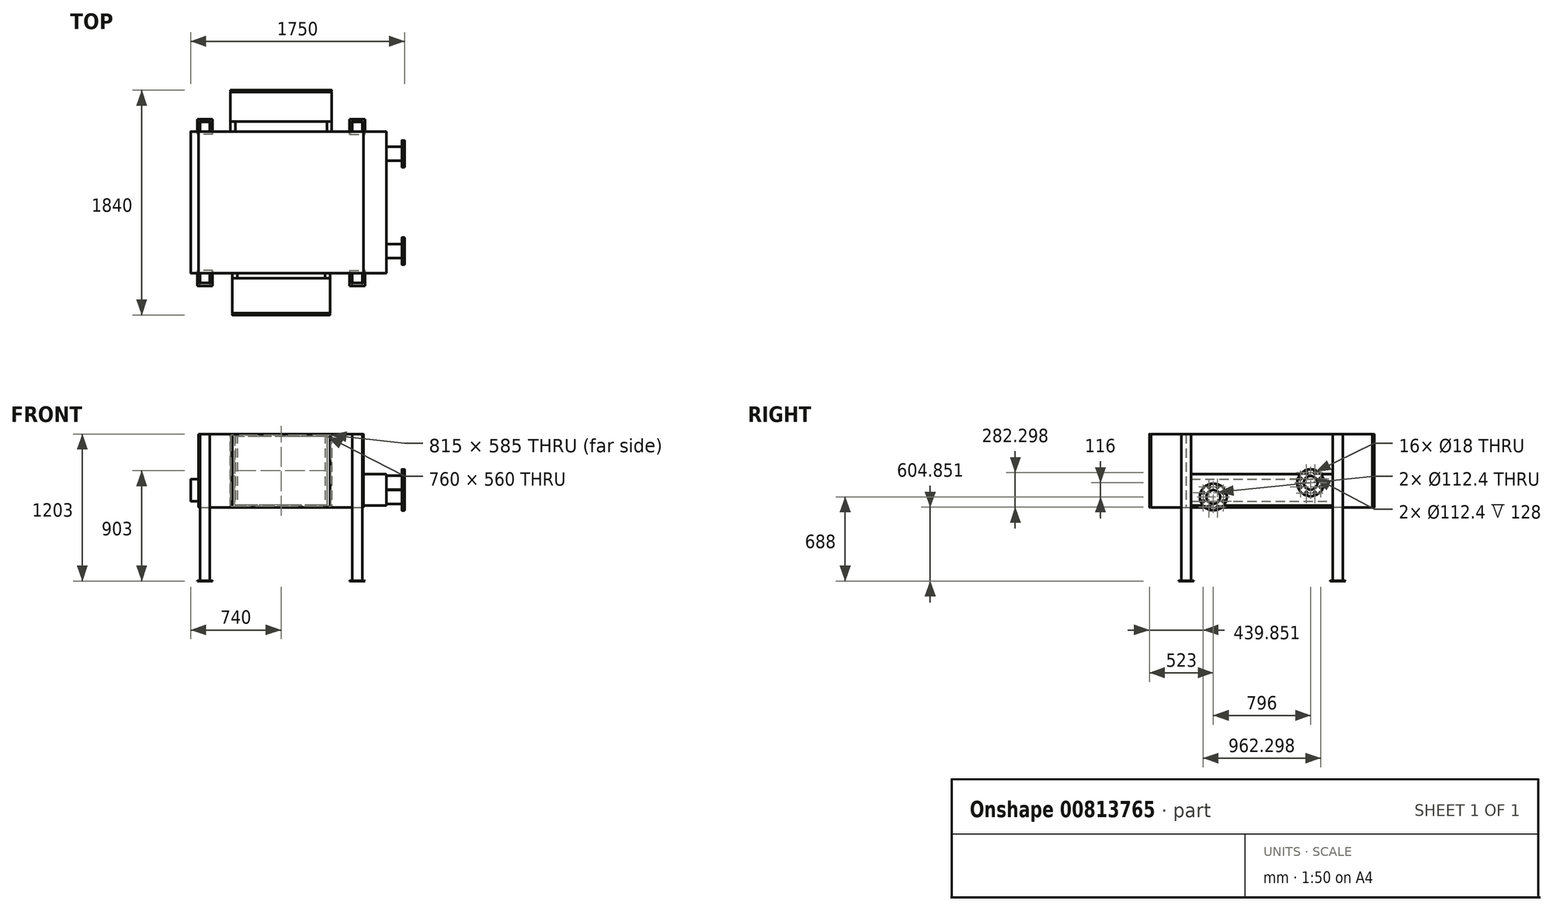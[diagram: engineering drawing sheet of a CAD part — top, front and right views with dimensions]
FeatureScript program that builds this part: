
annotation { "Feature Type Name" : "Feature", "Feature Type Description" : "" }
export const myFeature = defineFeature(function(context is Context, id is Id, definition is map)
    precondition{}
    {
        {
            var Q0;
            Q0=qCreatedBy(makeId("Top.planeOp"),FACE);
            var sketch = newSketch(context, id + "F0", { "sketchPlane" : qUnion([Q0])});
            skLineSegment(sketch, "E0.bottom", {"start": v(0, 0) * mm, "end": v(1350, 0) * mm});
            skLineSegment(sketch, "E0.top", {"start": v(0, 1160) * mm, "end": v(1350, 1160) * mm});
            skLineSegment(sketch, "E0.left", {"start": v(0, 0) * mm, "end": v(0, 1160) * mm});
            skLineSegment(sketch, "E0.right", {"start": v(1350, 0) * mm, "end": v(1350, 1160) * mm});
            skSolve(sketch);
        }
        {
            var Q0;
            Q0 = qSketchRegion(id + "F0", true);
            extrude(context, id + "F1", {"entities" : qUnion([Q0]), "depth" : 600 * mm, "offsetDistance" : 25 * mm});
        }
        {
            var Q0;
            Q0=makeQuery(id+"F1.opExtrude","SWEPT_FACE",FACE,{"disambiguationData":[OSD([sQuery(id+"F0.wireOp",EDGE,"E0.bottom")])]});
            var sketch = newSketch(context, id + "F2", { "sketchPlane" : qUnion([Q0])});
            skLineSegment(sketch, "E1.bottom", {"start": v(1258, -600) * mm, "end": v(1338, -600) * mm});
            skLineSegment(sketch, "E1.top", {"start": v(1258, 600) * mm, "end": v(1338, 600) * mm});
            skLineSegment(sketch, "E1.left", {"start": v(1258, -600) * mm, "end": v(1258, 600) * mm});
            skLineSegment(sketch, "E1.right", {"start": v(1338, -600) * mm, "end": v(1338, 600) * mm});
            skLineSegment(sketch, "E2", {"start": v(675, 600) * mm, "end": v(675, 2551.14) * mm, "construction": true});
            skLineSegment(sketch, "E3.MirrorCS", {"start": v(92, -600) * mm, "end": v(12, -600) * mm});
            skLineSegment(sketch, "E4.MirrorCS", {"start": v(92, 600) * mm, "end": v(12, 600) * mm});
            skLineSegment(sketch, "E5.MirrorCS", {"start": v(92, -600) * mm, "end": v(92, 600) * mm});
            skLineSegment(sketch, "E6.MirrorCS", {"start": v(12, -600) * mm, "end": v(12, 600) * mm});
            skSolve(sketch);
        }
        {
            var Q0;
            {var subQ0=sQuery(id+"F2.wireOp",EDGE,"E3.MirrorCS");Q0=makeQuery(id+"F2.imprint","IMPRINT",FACE,{"disambiguationData":[TD([[makeQuery(id+"F2.imprint","IMPRINT",EDGE,{"derivedFrom":subQ0}),-1.0]])]});}
            var Q1;
            {var subQ0=sQuery(id+"F2.wireOp",EDGE,"E1.bottom");Q1=makeQuery(id+"F2.imprint","IMPRINT",FACE,{"disambiguationData":[TD([[makeQuery(id+"F2.imprint","IMPRINT",EDGE,{"derivedFrom":subQ0}),1.0]])]});}
            var Q2;
            {var subQ0=sQuery(id+"F2.wireOp",EDGE,"E1.top");Q2=makeQuery(id+"F2.imprint","IMPRINT",FACE,{"disambiguationData":[TD([[makeQuery(id+"F2.imprint","IMPRINT",EDGE,{"derivedFrom":subQ0}),-1.0]])]});}
            var Q3;
            {var subQ0=sQuery(id+"F2.wireOp",EDGE,"E4.MirrorCS");Q3=makeQuery(id+"F2.imprint","IMPRINT",FACE,{"disambiguationData":[TD([[makeQuery(id+"F2.imprint","IMPRINT",EDGE,{"derivedFrom":subQ0}),-1.0]])]});}
            extrude(context, id + "F3", {"entities" : qUnion([Q0, Q1, Q2, Q3]), "depth" : 80 * mm, "offsetDistance" : 25 * mm});
        }
        {
            var Q0;
            Q0=makeQuery(id+"F1.opExtrude","CAP_EDGE",EDGE,{"disambiguationData":[OSD([sQuery(id+"F0.wireOp",EDGE,"E0.right")])],"isStart":false});
            cPlane(context, id + "F4", {"entities" : qUnion([Q0]), "cplaneType" : CPlaneType.MID_PLANE, "offset" : 25 * mm, "width" : 150 * mm, "height" : 150 * mm});
        }
        {
            var Q0;
            Q0=makeQuery(id+"F3.opExtrude","SWEPT_BODY",BODY,{"disambiguationData":[OSD([sQuery(id+"F2.wireOp",EDGE,"E3.MirrorCS"),sQuery(id+"F2.wireOp",EDGE,"E4.MirrorCS"),sQuery(id+"F2.wireOp",EDGE,"E5.MirrorCS"),sQuery(id+"F2.wireOp",EDGE,"E6.MirrorCS")])]});
            var Q1;
            Q1=makeQuery(id+"F3.opExtrude","SWEPT_BODY",BODY,{"disambiguationData":[OSD([sQuery(id+"F2.wireOp",EDGE,"E1.bottom"),sQuery(id+"F2.wireOp",EDGE,"E1.top"),sQuery(id+"F2.wireOp",EDGE,"E1.left"),sQuery(id+"F2.wireOp",EDGE,"E1.right")])]});
            var Q2;
            Q2=qCreatedBy(id+"F4.planeOp",FACE);
            mirror(context, id + "F5", {"entities" : qUnion([Q0, Q1]), "mirrorPlane" : qUnion([Q2])});
        }
        {
            var Q0;
            Q0=makeQuery(id+"F3.opExtrude","SWEPT_FACE",FACE,{"disambiguationData":[OSD([sQuery(id+"F2.wireOp",EDGE,"E1.bottom")])]});
            var sketch = newSketch(context, id + "F6", { "sketchPlane" : qUnion([Q0])});
            skLineSegment(sketch, "E7", {"start": v(1338, 80) * mm, "end": v(1258, 0) * mm, "construction": true});
            skLineSegment(sketch, "E8", {"start": v(1258, 0) * mm, "end": v(1338, 0) * mm, "construction": true});
            skLineSegment(sketch, "E9", {"start": v(1338, 0) * mm, "end": v(1258, 80) * mm, "construction": true});
            skLineSegment(sketch, "E10.0", {"start": v(1350, 0) * mm, "end": v(1350, -1160) * mm, "construction": true});
            skLineSegment(sketch, "E11.0", {"start": v(0, 0) * mm, "end": v(0, -1160) * mm, "construction": true});
            skLineSegment(sketch, "E12.0", {"start": v(0, -1160) * mm, "end": v(1350, -1160) * mm, "construction": true});
            skLineSegment(sketch, "E13.0", {"start": v(0, 0) * mm, "end": v(1350, 0) * mm, "construction": true});
            skLineSegment(sketch, "E14", {"start": v(675, -1160) * mm, "end": v(675, 174.46) * mm, "construction": true});
            skLineSegment(sketch, "E15", {"start": v(1350, -580) * mm, "end": v(-372.2, -580) * mm, "construction": true});
            skLineSegment(sketch, "E16.bottom", {"start": v(1235.5, -22.5) * mm, "end": v(1360.5, -22.5) * mm});
            skLineSegment(sketch, "E16.top", {"start": v(1235.5, 102.5) * mm, "end": v(1360.5, 102.5) * mm});
            skLineSegment(sketch, "E16.left", {"start": v(1235.5, -22.5) * mm, "end": v(1235.5, 102.5) * mm});
            skLineSegment(sketch, "E16.right", {"start": v(1360.5, -22.5) * mm, "end": v(1360.5, 102.5) * mm});
            skPoint(sketch, "E16.middle", {"position": v(1298, 40) * mm});
            skLineSegment(sketch, "E17.MirrorCS", {"start": v(1338, -1240) * mm, "end": v(1258, -1160) * mm, "construction": true});
            skLineSegment(sketch, "E18.MirrorCS", {"start": v(1235.5, -1137.5) * mm, "end": v(1360.5, -1137.5) * mm});
            skLineSegment(sketch, "E19.MirrorCS", {"start": v(1235.5, -1262.5) * mm, "end": v(1360.5, -1262.5) * mm});
            skLineSegment(sketch, "E20.MirrorCS", {"start": v(1235.5, -1137.5) * mm, "end": v(1235.5, -1262.5) * mm});
            skLineSegment(sketch, "E21.MirrorCS", {"start": v(1338, -1160) * mm, "end": v(1258, -1240) * mm, "construction": true});
            skLineSegment(sketch, "E22.MirrorCS", {"start": v(1258, -1160) * mm, "end": v(1338, -1160) * mm, "construction": true});
            skLineSegment(sketch, "E23.MirrorCS", {"start": v(1360.5, -1137.5) * mm, "end": v(1360.5, -1262.5) * mm});
            skPoint(sketch, "E24.MirrorP", {"position": v(1298, -1200) * mm});
            skLineSegment(sketch, "E25.MirrorCS", {"start": v(-10.5, -22.5) * mm, "end": v(-10.5, 102.5) * mm});
            skLineSegment(sketch, "E26.MirrorCS", {"start": v(114.5, 102.5) * mm, "end": v(-10.5, 102.5) * mm});
            skLineSegment(sketch, "E27.MirrorCS", {"start": v(114.5, -22.5) * mm, "end": v(-10.5, -22.5) * mm});
            skLineSegment(sketch, "E28.MirrorCS", {"start": v(12, 0) * mm, "end": v(92, 80) * mm, "construction": true});
            skLineSegment(sketch, "E29.MirrorCS", {"start": v(92, 0) * mm, "end": v(12, 0) * mm, "construction": true});
            skLineSegment(sketch, "E30.MirrorCS", {"start": v(12, 80) * mm, "end": v(92, 0) * mm, "construction": true});
            skLineSegment(sketch, "E31.MirrorCS", {"start": v(114.5, -1137.5) * mm, "end": v(114.5, -1262.5) * mm});
            skLineSegment(sketch, "E32.MirrorCS", {"start": v(114.5, -1137.5) * mm, "end": v(-10.5, -1137.5) * mm});
            skLineSegment(sketch, "E33.MirrorCS", {"start": v(92, -1160) * mm, "end": v(12, -1160) * mm, "construction": true});
            skLineSegment(sketch, "E34.MirrorCS", {"start": v(-10.5, -1137.5) * mm, "end": v(-10.5, -1262.5) * mm});
            skLineSegment(sketch, "E35.MirrorCS", {"start": v(114.5, -22.5) * mm, "end": v(114.5, 102.5) * mm});
            skLineSegment(sketch, "E36.MirrorCS", {"start": v(12, -1160) * mm, "end": v(92, -1240) * mm, "construction": true});
            skPoint(sketch, "E37.MirrorP", {"position": v(52, 40) * mm});
            skLineSegment(sketch, "E38.MirrorCS", {"start": v(114.5, -1262.5) * mm, "end": v(-10.5, -1262.5) * mm});
            skLineSegment(sketch, "E39.MirrorCS", {"start": v(12, -1240) * mm, "end": v(92, -1160) * mm, "construction": true});
            skPoint(sketch, "E40.MirrorP", {"position": v(52, -1200) * mm});
            skSolve(sketch);
        }
        {
            var Q0;
            Q0 = qSketchRegion(id + "F6", true);
            extrude(context, id + "F7", {"entities" : qUnion([Q0]), "operationType" : NewBodyOperationType.ADD, "depth" : 3 * mm, "offsetDistance" : 25 * mm});
        }
        {
            var Q0;
            Q0=makeQuery(id+"F1.opExtrude","SWEPT_FACE",FACE,{"disambiguationData":[OSD([sQuery(id+"F0.wireOp",EDGE,"E0.bottom")])]});
            var sketch = newSketch(context, id + "F8", { "sketchPlane" : qUnion([Q0])});
            skLineSegment(sketch, "E41", {"start": v(675, 600) * mm, "end": v(675, 0) * mm, "construction": true});
            skLineSegment(sketch, "E42.bottom", {"start": v(1075, 600) * mm, "end": v(275, 600) * mm});
            skLineSegment(sketch, "E42.top", {"start": v(1075, 0) * mm, "end": v(275, 0) * mm});
            skLineSegment(sketch, "E42.left", {"start": v(1075, 600) * mm, "end": v(1075, 0) * mm});
            skLineSegment(sketch, "E42.right", {"start": v(275, 600) * mm, "end": v(275, 0) * mm});
            skPoint(sketch, "E42.middle", {"position": v(675, 300) * mm});
            skLineSegment(sketch, "E43.0", {"start": v(316, 600) * mm, "end": v(316, 0) * mm});
            skLineSegment(sketch, "E44.0", {"start": v(-5, -5) * mm, "end": v(1355, -5) * mm});
            skLineSegment(sketch, "E44.1", {"start": v(-5, 605) * mm, "end": v(-5, -5) * mm});
            skLineSegment(sketch, "E44.2", {"start": v(1355, 605) * mm, "end": v(-5, 605) * mm});
            skLineSegment(sketch, "E44.3", {"start": v(1355, -5) * mm, "end": v(1355, 605) * mm});
            skLineSegment(sketch, "E45.0", {"start": v(1034, 600) * mm, "end": v(1034, 0) * mm});
            skSolve(sketch);
        }
        {
            var Q0;
            {var subQ0=sQuery(id+"F8.wireOp",EDGE,"E42.right");Q0=makeQuery(id+"F8.imprint","IMPRINT",FACE,{"disambiguationData":[TD([[makeQuery(id+"F8.imprint","IMPRINT",EDGE,{"derivedFrom":subQ0}),1.0]])]});}
            var Q1;
            {var subQ0=sQuery(id+"F8.wireOp",EDGE,"E42.left");Q1=makeQuery(id+"F8.imprint","IMPRINT",FACE,{"disambiguationData":[TD([[makeQuery(id+"F8.imprint","IMPRINT",EDGE,{"derivedFrom":subQ0}),-1.0]])]});}
            extrude(context, id + "F9", {"entities" : qUnion([Q0, Q1]), "depth" : 41 * mm, "offsetDistance" : 25 * mm});
        }
        {
            var Q0;
            Q0=makeQuery(id+"F9.opExtrude","CAP_FACE",FACE,{"disambiguationData":[OSD([sQuery(id+"F8.wireOp",EDGE,"E42.bottom"),sQuery(id+"F8.wireOp",EDGE,"E42.top"),sQuery(id+"F8.wireOp",EDGE,"E42.right"),sQuery(id+"F8.wireOp",EDGE,"E43.0")])],"isStart":false});
            var sketch = newSketch(context, id + "F10", { "sketchPlane" : qUnion([Q0])});
            skLineSegment(sketch, "E46.bottom", {"start": v(275, 600) * mm, "end": v(1075, 600) * mm});
            skLineSegment(sketch, "E46.top", {"start": v(275, 0) * mm, "end": v(1075, 0) * mm});
            skLineSegment(sketch, "E46.left", {"start": v(275, 600) * mm, "end": v(275, 0) * mm});
            skLineSegment(sketch, "E46.right", {"start": v(1075, 600) * mm, "end": v(1075, 0) * mm});
            skSolve(sketch);
        }
        {
            var Q0;
            Q0 = qSketchRegion(id + "F10", true);
            extrude(context, id + "F11", {"entities" : qUnion([Q0]), "depth" : 277 * mm, "offsetDistance" : 25 * mm});
        }
        {
            var Q0;
            Q0=makeQuery(id+"F11.opExtrude","CAP_FACE",FACE,{"disambiguationData":[OSD([sQuery(id+"F10.wireOp",EDGE,"E46.bottom"),sQuery(id+"F10.wireOp",EDGE,"E46.top"),sQuery(id+"F10.wireOp",EDGE,"E46.left"),sQuery(id+"F10.wireOp",EDGE,"E46.right")])],"isStart":false});
            var sketch = newSketch(context, id + "F12", { "sketchPlane" : qUnion([Q0])});
            skLineSegment(sketch, "E47.bottom", {"start": v(275, 600) * mm, "end": v(1075, 600) * mm});
            skLineSegment(sketch, "E47.top", {"start": v(275, 0) * mm, "end": v(1075, 0) * mm});
            skLineSegment(sketch, "E47.left", {"start": v(275, 600) * mm, "end": v(275, 0) * mm});
            skLineSegment(sketch, "E47.right", {"start": v(1075, 600) * mm, "end": v(1075, 0) * mm});
            skSolve(sketch);
        }
        {
            var Q0;
            Q0 = qSketchRegion(id + "F12", true);
            extrude(context, id + "F13", {"entities" : qUnion([Q0]), "operationType" : NewBodyOperationType.ADD, "depth" : 23 * mm, "offsetDistance" : 25 * mm});
        }
        {
            var Q0;
            Q0=makeQuery(id+"F13.opExtrude","CAP_FACE",FACE,{"disambiguationData":[OSD([sQuery(id+"F12.wireOp",EDGE,"E47.bottom"),sQuery(id+"F12.wireOp",EDGE,"E47.top"),sQuery(id+"F12.wireOp",EDGE,"E47.left"),sQuery(id+"F12.wireOp",EDGE,"E47.right")])],"isStart":false});
            cPlane(context, id + "F14", {"entities" : qUnion([Q0]), "cplaneType" : CPlaneType.OFFSET, "offset" : 7.5 * mm, "oppositeDirection" : true, "width" : 150 * mm, "height" : 150 * mm});
        }
        {
            var Q0;
            Q0=qCreatedBy(id+"F14.planeOp",FACE);
            var sketch = newSketch(context, id + "F15", { "sketchPlane" : qUnion([Q0])});
            skLineSegment(sketch, "E48.0", {"start": v(295, 580) * mm, "end": v(295, 20) * mm});
            skLineSegment(sketch, "E48.1", {"start": v(1055, 580) * mm, "end": v(295, 580) * mm});
            skLineSegment(sketch, "E48.2", {"start": v(1055, 20) * mm, "end": v(1055, 580) * mm});
            skLineSegment(sketch, "E48.3", {"start": v(295, 20) * mm, "end": v(1055, 20) * mm});
            skLineSegment(sketch, "E49.0.0", {"start": v(275, 600) * mm, "end": v(275, 0) * mm});
            skLineSegment(sketch, "E49.0.1", {"start": v(275, 0) * mm, "end": v(1075, 0) * mm});
            skLineSegment(sketch, "E49.0.2", {"start": v(1075, 0) * mm, "end": v(1075, 600) * mm});
            skLineSegment(sketch, "E49.0.3", {"start": v(1075, 600) * mm, "end": v(275, 600) * mm});
            skSolve(sketch);
        }
        {
            var Q0;
            Q0=makeQuery(id+"F15.imprint","IMPRINT",FACE,{"disambiguationData":[TD([[makeQuery(id+"F15.imprint","IMPRINT",EDGE,{"derivedFrom":sQuery(id+"F15.wireOp",EDGE,"E48.0")}),-1.0]])]});
            extrude(context, id + "F16", {"entities" : qUnion([Q0]), "operationType" : NewBodyOperationType.REMOVE, "oppositeDirection" : true, "depth" : 7.5 * mm, "offsetDistance" : 25 * mm});
        }
        {
            var Q0;
            Q0=makeQuery(id+"F1.opExtrude","SWEPT_FACE",FACE,{"disambiguationData":[OSD([sQuery(id+"F0.wireOp",EDGE,"E0.top")])]});
            var sketch = newSketch(context, id + "F17", { "sketchPlane" : qUnion([Q0])});
            skLineSegment(sketch, "E50", {"start": v(-675, 0) * mm, "end": v(-675, 783.43) * mm, "construction": true});
            skLineSegment(sketch, "E51.bottom", {"start": v(-1090, 600) * mm, "end": v(-1049, 600) * mm});
            skLineSegment(sketch, "E51.top", {"start": v(-1090, 0) * mm, "end": v(-1049, 0) * mm});
            skLineSegment(sketch, "E51.left", {"start": v(-1090, 600) * mm, "end": v(-1090, 0) * mm});
            skLineSegment(sketch, "E51.right", {"start": v(-1049, 600) * mm, "end": v(-1049, 0) * mm});
            skLineSegment(sketch, "E52.MirrorCS", {"start": v(-301, 600) * mm, "end": v(-301, 0) * mm});
            skLineSegment(sketch, "E53.MirrorCS", {"start": v(-260, 600) * mm, "end": v(-260, 0) * mm});
            skLineSegment(sketch, "E54.MirrorCS", {"start": v(-260, 0) * mm, "end": v(-301, 0) * mm});
            skLineSegment(sketch, "E55.MirrorCS", {"start": v(-260, 600) * mm, "end": v(-301, 600) * mm});
            skSolve(sketch);
        }
        {
            var Q0;
            Q0=makeQuery(id+"F17.imprint","IMPRINT",FACE,{"disambiguationData":[TD([[makeQuery(id+"F17.imprint","IMPRINT",EDGE,{"derivedFrom":sQuery(id+"F17.wireOp",EDGE,"E51.bottom")}),1.0]])]});
            var Q1;
            Q1=makeQuery(id+"F17.imprint","IMPRINT",FACE,{"disambiguationData":[TD([[makeQuery(id+"F17.imprint","IMPRINT",EDGE,{"derivedFrom":sQuery(id+"F17.wireOp",EDGE,"E52.MirrorCS")}),1.0]])]});
            extrude(context, id + "F18", {"entities" : qUnion([Q0, Q1]), "depth" : 81 * mm, "offsetDistance" : 25 * mm});
        }
        {
            var Q0;
            Q0=makeQuery(id+"F18.opExtrude","CAP_FACE",FACE,{"disambiguationData":[OSD([sQuery(id+"F17.wireOp",EDGE,"E51.bottom"),sQuery(id+"F17.wireOp",EDGE,"E51.top"),sQuery(id+"F17.wireOp",EDGE,"E51.left"),sQuery(id+"F17.wireOp",EDGE,"E51.right")])],"isStart":false});
            var sketch = newSketch(context, id + "F19", { "sketchPlane" : qUnion([Q0])});
            skLineSegment(sketch, "E56.bottom", {"start": v(-1090, 600) * mm, "end": v(-260, 600) * mm});
            skLineSegment(sketch, "E56.top", {"start": v(-1090, 0) * mm, "end": v(-260, 0) * mm});
            skLineSegment(sketch, "E56.left", {"start": v(-1090, 600) * mm, "end": v(-1090, 0) * mm});
            skLineSegment(sketch, "E56.right", {"start": v(-260, 600) * mm, "end": v(-260, 0) * mm});
            skSolve(sketch);
        }
        {
            var Q0;
            Q0 = qSketchRegion(id + "F19", true);
            extrude(context, id + "F20", {"entities" : qUnion([Q0]), "depth" : 258 * mm, "offsetDistance" : 25 * mm});
        }
        {
            var Q0;
            Q0=makeQuery(id+"F20.opExtrude","CAP_FACE",FACE,{"disambiguationData":[OSD([sQuery(id+"F19.wireOp",EDGE,"E56.bottom"),sQuery(id+"F19.wireOp",EDGE,"E56.top"),sQuery(id+"F19.wireOp",EDGE,"E56.left"),sQuery(id+"F19.wireOp",EDGE,"E56.right")])],"isStart":false});
            cPlane(context, id + "F21", {"entities" : qUnion([Q0]), "cplaneType" : CPlaneType.OFFSET, "offset" : 7.5 * mm, "oppositeDirection" : true, "width" : 150 * mm, "height" : 150 * mm});
        }
        {
            var Q0;
            Q0=qCreatedBy(id+"F21.planeOp",FACE);
            var sketch = newSketch(context, id + "F22", { "sketchPlane" : qUnion([Q0])});
            skLineSegment(sketch, "E57.0.0", {"start": v(-260, 600) * mm, "end": v(-1090, 600) * mm});
            skLineSegment(sketch, "E57.0.1", {"start": v(-1090, 600) * mm, "end": v(-1090, 0) * mm});
            skLineSegment(sketch, "E57.0.2", {"start": v(-1090, 0) * mm, "end": v(-260, 0) * mm});
            skLineSegment(sketch, "E57.0.3", {"start": v(-260, 0) * mm, "end": v(-260, 600) * mm});
            skLineSegment(sketch, "E58.0", {"start": v(-267.5, 592.5) * mm, "end": v(-1082.5, 592.5) * mm});
            skLineSegment(sketch, "E58.1", {"start": v(-267.5, 7.5) * mm, "end": v(-267.5, 592.5) * mm});
            skLineSegment(sketch, "E58.2", {"start": v(-1082.5, 7.5) * mm, "end": v(-267.5, 7.5) * mm});
            skLineSegment(sketch, "E58.3", {"start": v(-1082.5, 592.5) * mm, "end": v(-1082.5, 7.5) * mm});
            skSolve(sketch);
        }
        {
            var Q0;
            Q0=makeQuery(id+"F22.imprint","IMPRINT",FACE,{"disambiguationData":[TD([[makeQuery(id+"F22.imprint","IMPRINT",EDGE,{"derivedFrom":sQuery(id+"F22.wireOp",EDGE,"E57.0.0")}),1.0]])]});
            extrude(context, id + "F23", {"entities" : qUnion([Q0]), "operationType" : NewBodyOperationType.REMOVE, "oppositeDirection" : true, "depth" : 7.5 * mm, "offsetDistance" : 25 * mm});
        }
        {
            var Q0;
            Q0=makeQuery(id+"F13.opExtrude","CAP_EDGE",EDGE,{"disambiguationData":[OSD([sQuery(id+"F12.wireOp",EDGE,"E47.left")])],"isStart":false});
            var Q1;
            Q1=makeQuery(id+"F13.opExtrude","CAP_EDGE",EDGE,{"disambiguationData":[OSD([sQuery(id+"F12.wireOp",EDGE,"E47.bottom")])],"isStart":false});
            var Q2;
            Q2=makeQuery(id+"F13.opExtrude","CAP_EDGE",EDGE,{"disambiguationData":[OSD([sQuery(id+"F12.wireOp",EDGE,"E47.top")])],"isStart":false});
            var Q3;
            Q3=makeQuery(id+"F13.opExtrude","CAP_EDGE",EDGE,{"disambiguationData":[OSD([sQuery(id+"F12.wireOp",EDGE,"E47.right")])],"isStart":false});
            var Q4;
            Q4=makeQuery(id+"F20.opExtrude","CAP_EDGE",EDGE,{"disambiguationData":[OSD([sQuery(id+"F19.wireOp",EDGE,"E56.left")])],"isStart":false});
            var Q5;
            Q5=makeQuery(id+"F20.opExtrude","CAP_EDGE",EDGE,{"disambiguationData":[OSD([sQuery(id+"F19.wireOp",EDGE,"E56.bottom")])],"isStart":false});
            var Q6;
            Q6=makeQuery(id+"F20.opExtrude","CAP_EDGE",EDGE,{"disambiguationData":[OSD([sQuery(id+"F19.wireOp",EDGE,"E56.right")])],"isStart":false});
            var Q7;
            Q7=makeQuery(id+"F20.opExtrude","CAP_EDGE",EDGE,{"disambiguationData":[OSD([sQuery(id+"F19.wireOp",EDGE,"E56.top")])],"isStart":false});
            fillet(context, id + "F24", {"entities" : qUnion([Q0, Q1, Q2, Q3, Q4, Q5, Q6, Q7]), "radius" : 2 * mm, "tangentPropagation" : true, "allowEdgeOverflow" : false});
        }
        {
            var Q0;
            {var subQ0=sQuery(id+"F19.wireOp",EDGE,"E56.bottom");var subQ1=sQuery(id+"F19.wireOp",EDGE,"E56.left");Q0=makeQuery(id+"F23.boolean.opBoolean","SPLIT",EDGE,{"disambiguationData":[TD([makeQuery(id+"F20.opExtrude","CAP_FACE",FACE,{"disambiguationData":[OSD([subQ0,sQuery(id+"F19.wireOp",EDGE,"E56.top"),subQ1,sQuery(id+"F19.wireOp",EDGE,"E56.right")])],"isStart":true})])],"derivedFrom":makeQuery(id+"F20.opExtrude","SWEPT_EDGE",EDGE,{"disambiguationData":[OSD([subQ0,subQ1])]})});}
            var Q1;
            {var subQ0=sQuery(id+"F19.wireOp",EDGE,"E56.left");var subQ1=sQuery(id+"F19.wireOp",EDGE,"E56.top");Q1=makeQuery(id+"F23.boolean.opBoolean","SPLIT",EDGE,{"disambiguationData":[TD([makeQuery(id+"F20.opExtrude","CAP_FACE",FACE,{"disambiguationData":[OSD([sQuery(id+"F19.wireOp",EDGE,"E56.bottom"),subQ1,subQ0,sQuery(id+"F19.wireOp",EDGE,"E56.right")])],"isStart":true})])],"derivedFrom":makeQuery(id+"F20.opExtrude","SWEPT_EDGE",EDGE,{"disambiguationData":[OSD([subQ1,subQ0])]})});}
            var Q2;
            {var subQ0=sQuery(id+"F19.wireOp",EDGE,"E56.right");var subQ1=sQuery(id+"F19.wireOp",EDGE,"E56.top");Q2=makeQuery(id+"F23.boolean.opBoolean","SPLIT",EDGE,{"disambiguationData":[TD([makeQuery(id+"F20.opExtrude","CAP_FACE",FACE,{"disambiguationData":[OSD([sQuery(id+"F19.wireOp",EDGE,"E56.bottom"),subQ1,sQuery(id+"F19.wireOp",EDGE,"E56.left"),subQ0])],"isStart":true})])],"derivedFrom":makeQuery(id+"F20.opExtrude","SWEPT_EDGE",EDGE,{"disambiguationData":[OSD([subQ1,subQ0])]})});}
            var Q3;
            {var subQ0=sQuery(id+"F19.wireOp",EDGE,"E56.bottom");var subQ1=sQuery(id+"F19.wireOp",EDGE,"E56.right");Q3=makeQuery(id+"F23.boolean.opBoolean","SPLIT",EDGE,{"disambiguationData":[TD([makeQuery(id+"F20.opExtrude","CAP_FACE",FACE,{"disambiguationData":[OSD([subQ0,sQuery(id+"F19.wireOp",EDGE,"E56.top"),sQuery(id+"F19.wireOp",EDGE,"E56.left"),subQ1])],"isStart":true})])],"derivedFrom":makeQuery(id+"F20.opExtrude","SWEPT_EDGE",EDGE,{"disambiguationData":[OSD([subQ0,subQ1])]})});}
            var Q4;
            {var subQ0=sQuery(id+"F12.wireOp",EDGE,"E47.bottom");var subQ1=sQuery(id+"F10.wireOp",EDGE,"E46.left");var subQ2=sQuery(id+"F10.wireOp",EDGE,"E46.bottom");var subQ3=sQuery(id+"F12.wireOp",EDGE,"E47.left");Q4=makeQuery(id+"F16.boolean.opBoolean","SPLIT",EDGE,{"disambiguationData":[TD([makeQuery(id+"F11.opExtrude","CAP_FACE",FACE,{"disambiguationData":[OSD([subQ2,sQuery(id+"F10.wireOp",EDGE,"E46.top"),subQ1,sQuery(id+"F10.wireOp",EDGE,"E46.right")])],"isStart":true})])],"derivedFrom":makeQuery(id+"F13.boolean.opBoolean","MERGE",EDGE,{"derivedFrom":[makeQuery(id+"F11.opExtrude","SWEPT_EDGE",EDGE,{"disambiguationData":[OSD([subQ2,subQ1])]}),makeQuery(id+"F13.opExtrude","SWEPT_EDGE",EDGE,{"disambiguationData":[OSD([subQ0,subQ3])]})]})});}
            var Q5;
            {var subQ0=sQuery(id+"F12.wireOp",EDGE,"E47.bottom");var subQ1=sQuery(id+"F10.wireOp",EDGE,"E46.right");var subQ2=sQuery(id+"F10.wireOp",EDGE,"E46.bottom");var subQ3=sQuery(id+"F12.wireOp",EDGE,"E47.right");Q5=makeQuery(id+"F16.boolean.opBoolean","SPLIT",EDGE,{"disambiguationData":[TD([makeQuery(id+"F11.opExtrude","CAP_FACE",FACE,{"disambiguationData":[OSD([subQ2,sQuery(id+"F10.wireOp",EDGE,"E46.top"),sQuery(id+"F10.wireOp",EDGE,"E46.left"),subQ1])],"isStart":true})])],"derivedFrom":makeQuery(id+"F13.boolean.opBoolean","MERGE",EDGE,{"derivedFrom":[makeQuery(id+"F11.opExtrude","SWEPT_EDGE",EDGE,{"disambiguationData":[OSD([subQ2,subQ1])]}),makeQuery(id+"F13.opExtrude","SWEPT_EDGE",EDGE,{"disambiguationData":[OSD([subQ0,subQ3])]})]})});}
            var Q6;
            {var subQ0=sQuery(id+"F10.wireOp",EDGE,"E46.left");var subQ1=sQuery(id+"F12.wireOp",EDGE,"E47.top");var subQ2=sQuery(id+"F10.wireOp",EDGE,"E46.top");var subQ3=sQuery(id+"F12.wireOp",EDGE,"E47.left");Q6=makeQuery(id+"F16.boolean.opBoolean","SPLIT",EDGE,{"disambiguationData":[TD([makeQuery(id+"F11.opExtrude","CAP_FACE",FACE,{"disambiguationData":[OSD([sQuery(id+"F10.wireOp",EDGE,"E46.bottom"),subQ2,subQ0,sQuery(id+"F10.wireOp",EDGE,"E46.right")])],"isStart":true})])],"derivedFrom":makeQuery(id+"F13.boolean.opBoolean","MERGE",EDGE,{"derivedFrom":[makeQuery(id+"F11.opExtrude","SWEPT_EDGE",EDGE,{"disambiguationData":[OSD([subQ2,subQ0])]}),makeQuery(id+"F13.opExtrude","SWEPT_EDGE",EDGE,{"disambiguationData":[OSD([subQ1,subQ3])]})]})});}
            var Q7;
            {var subQ0=sQuery(id+"F10.wireOp",EDGE,"E46.right");var subQ1=sQuery(id+"F10.wireOp",EDGE,"E46.top");var subQ2=sQuery(id+"F12.wireOp",EDGE,"E47.top");var subQ3=sQuery(id+"F12.wireOp",EDGE,"E47.right");Q7=makeQuery(id+"F16.boolean.opBoolean","SPLIT",EDGE,{"disambiguationData":[TD([makeQuery(id+"F11.opExtrude","CAP_FACE",FACE,{"disambiguationData":[OSD([sQuery(id+"F10.wireOp",EDGE,"E46.bottom"),subQ1,sQuery(id+"F10.wireOp",EDGE,"E46.left"),subQ0])],"isStart":true})])],"derivedFrom":makeQuery(id+"F13.boolean.opBoolean","MERGE",EDGE,{"derivedFrom":[makeQuery(id+"F11.opExtrude","SWEPT_EDGE",EDGE,{"disambiguationData":[OSD([subQ1,subQ0])]}),makeQuery(id+"F13.opExtrude","SWEPT_EDGE",EDGE,{"disambiguationData":[OSD([subQ2,subQ3])]})]})});}
            fillet(context, id + "F25", {"entities" : qUnion([Q0, Q1, Q2, Q3, Q4, Q5, Q6, Q7]), "radius" : 3 * mm, "tangentPropagation" : true, "allowEdgeOverflow" : false});
        }
        {
            var Q0;
            Q0=makeQuery(id+"F16.boolean.opBoolean","COPY",EDGE,{"derivedFrom":makeQuery(id+"F16.opExtrude","CAP_EDGE",EDGE,{"disambiguationData":[OSD([sQuery(id+"F15.wireOp",EDGE,"E49.0.3")])],"isStart":false})});
            var Q1;
            Q1=makeQuery(id+"F16.boolean.opBoolean","COPY",EDGE,{"derivedFrom":makeQuery(id+"F16.opExtrude","CAP_EDGE",EDGE,{"disambiguationData":[OSD([sQuery(id+"F15.wireOp",EDGE,"E49.0.2")])],"isStart":false})});
            var Q2;
            Q2=makeQuery(id+"F16.boolean.opBoolean","COPY",EDGE,{"derivedFrom":makeQuery(id+"F16.opExtrude","CAP_EDGE",EDGE,{"disambiguationData":[OSD([sQuery(id+"F15.wireOp",EDGE,"E49.0.0")])],"isStart":true})});
            var Q3;
            Q3=makeQuery(id+"F16.boolean.opBoolean","COPY",EDGE,{"derivedFrom":makeQuery(id+"F16.opExtrude","CAP_EDGE",EDGE,{"disambiguationData":[OSD([sQuery(id+"F15.wireOp",EDGE,"E49.0.1")])],"isStart":true})});
            var Q4;
            Q4=makeQuery(id+"F16.boolean.opBoolean","COPY",EDGE,{"derivedFrom":makeQuery(id+"F16.opExtrude","CAP_EDGE",EDGE,{"disambiguationData":[OSD([sQuery(id+"F15.wireOp",EDGE,"E49.0.3")])],"isStart":true})});
            var Q5;
            Q5=makeQuery(id+"F16.boolean.opBoolean","COPY",EDGE,{"derivedFrom":makeQuery(id+"F16.opExtrude","CAP_EDGE",EDGE,{"disambiguationData":[OSD([sQuery(id+"F15.wireOp",EDGE,"E49.0.2")])],"isStart":true})});
            var Q6;
            Q6=makeQuery(id+"F23.boolean.opBoolean","COPY",EDGE,{"derivedFrom":makeQuery(id+"F23.opExtrude","CAP_EDGE",EDGE,{"disambiguationData":[OSD([sQuery(id+"F22.wireOp",EDGE,"E57.0.0")])],"isStart":false})});
            var Q7;
            Q7=makeQuery(id+"F23.boolean.opBoolean","COPY",EDGE,{"derivedFrom":makeQuery(id+"F23.opExtrude","CAP_EDGE",EDGE,{"disambiguationData":[OSD([sQuery(id+"F22.wireOp",EDGE,"E57.0.0")])],"isStart":true})});
            var Q8;
            Q8=makeQuery(id+"F23.boolean.opBoolean","COPY",EDGE,{"derivedFrom":makeQuery(id+"F23.opExtrude","CAP_EDGE",EDGE,{"disambiguationData":[OSD([sQuery(id+"F22.wireOp",EDGE,"E57.0.3")])],"isStart":true})});
            var Q9;
            Q9=makeQuery(id+"F23.boolean.opBoolean","COPY",EDGE,{"derivedFrom":makeQuery(id+"F23.opExtrude","CAP_EDGE",EDGE,{"disambiguationData":[OSD([sQuery(id+"F22.wireOp",EDGE,"E57.0.1")])],"isStart":true})});
            var Q10;
            Q10=makeQuery(id+"F23.boolean.opBoolean","COPY",EDGE,{"derivedFrom":makeQuery(id+"F23.opExtrude","CAP_EDGE",EDGE,{"disambiguationData":[OSD([sQuery(id+"F22.wireOp",EDGE,"E57.0.2")])],"isStart":true})});
            fillet(context, id + "F26", {"entities" : qUnion([Q0, Q1, Q2, Q3, Q4, Q5, Q6, Q7, Q8, Q9, Q10]), "radius" : 2 * mm, "tangentPropagation" : true, "allowEdgeOverflow" : false});
        }
        {
            var Q0;
            Q0=makeQuery(id+"F7.opExtrude","CAP_FACE",FACE,{"disambiguationData":[OSD([sQuery(id+"F6.wireOp",EDGE,"E18.MirrorCS"),sQuery(id+"F6.wireOp",EDGE,"E19.MirrorCS"),sQuery(id+"F6.wireOp",EDGE,"E20.MirrorCS"),sQuery(id+"F6.wireOp",EDGE,"E23.MirrorCS")])],"isStart":true});
            var Q1;
            Q1=makeQuery(id+"F7.opExtrude","CAP_FACE",FACE,{"disambiguationData":[OSD([sQuery(id+"F6.wireOp",EDGE,"E16.bottom"),sQuery(id+"F6.wireOp",EDGE,"E16.top"),sQuery(id+"F6.wireOp",EDGE,"E16.left"),sQuery(id+"F6.wireOp",EDGE,"E16.right")])],"isStart":true});
            var Q2;
            Q2=makeQuery(id+"F7.opExtrude","CAP_FACE",FACE,{"disambiguationData":[OSD([sQuery(id+"F6.wireOp",EDGE,"E31.MirrorCS"),sQuery(id+"F6.wireOp",EDGE,"E32.MirrorCS"),sQuery(id+"F6.wireOp",EDGE,"E34.MirrorCS"),sQuery(id+"F6.wireOp",EDGE,"E38.MirrorCS")])],"isStart":true});
            var Q3;
            Q3=makeQuery(id+"F7.opExtrude","CAP_FACE",FACE,{"disambiguationData":[OSD([sQuery(id+"F6.wireOp",EDGE,"E25.MirrorCS"),sQuery(id+"F6.wireOp",EDGE,"E26.MirrorCS"),sQuery(id+"F6.wireOp",EDGE,"E27.MirrorCS"),sQuery(id+"F6.wireOp",EDGE,"E35.MirrorCS")])],"isStart":true});
            fillet(context, id + "F27", {"entities" : qUnion([Q0, Q1, Q2, Q3]), "radius" : 6 * mm, "tangentPropagation" : true, "allowEdgeOverflow" : false});
        }
        {
            var Q0;
            Q0=makeQuery(id+"F5.opPattern","COPY",EDGE,{"derivedFrom":makeQuery(id+"F3.opExtrude","CAP_EDGE",EDGE,{"disambiguationData":[OSD([sQuery(id+"F2.wireOp",EDGE,"E6.MirrorCS")])],"isStart":false}),"instanceName":"1"});
            var Q1;
            Q1=makeQuery(id+"F5.opPattern","COPY",EDGE,{"derivedFrom":makeQuery(id+"F3.opExtrude","CAP_EDGE",EDGE,{"disambiguationData":[OSD([sQuery(id+"F2.wireOp",EDGE,"E5.MirrorCS")])],"isStart":false}),"instanceName":"1"});
            var Q2;
            Q2=makeQuery(id+"F5.opPattern","COPY",EDGE,{"derivedFrom":makeQuery(id+"F3.opExtrude","CAP_EDGE",EDGE,{"disambiguationData":[OSD([sQuery(id+"F2.wireOp",EDGE,"E4.MirrorCS")])],"isStart":false}),"instanceName":"1"});
            var Q3;
            Q3=makeQuery(id+"F5.opPattern","COPY",EDGE,{"derivedFrom":makeQuery(id+"F3.opExtrude","SWEPT_EDGE",EDGE,{"disambiguationData":[OSD([sQuery(id+"F0.wireOp",EDGE,"E0.bottom"),sQuery(id+"F2.wireOp",EDGE,"E4.MirrorCS"),sQuery(id+"F2.wireOp",EDGE,"E6.MirrorCS")])]}),"instanceName":"1"});
            var Q4;
            Q4=makeQuery(id+"F5.opPattern","COPY",EDGE,{"derivedFrom":makeQuery(id+"F3.opExtrude","SWEPT_EDGE",EDGE,{"disambiguationData":[OSD([sQuery(id+"F0.wireOp",EDGE,"E0.bottom"),sQuery(id+"F2.wireOp",EDGE,"E4.MirrorCS"),sQuery(id+"F2.wireOp",EDGE,"E5.MirrorCS")])]}),"instanceName":"1"});
            var Q5;
            Q5=makeQuery(id+"F3.opExtrude","CAP_EDGE",EDGE,{"disambiguationData":[OSD([sQuery(id+"F2.wireOp",EDGE,"E6.MirrorCS")])],"isStart":false});
            var Q6;
            Q6=makeQuery(id+"F3.opExtrude","CAP_EDGE",EDGE,{"disambiguationData":[OSD([sQuery(id+"F2.wireOp",EDGE,"E5.MirrorCS")])],"isStart":false});
            var Q7;
            Q7=makeQuery(id+"F3.opExtrude","SWEPT_EDGE",EDGE,{"disambiguationData":[OSD([sQuery(id+"F0.wireOp",EDGE,"E0.bottom"),sQuery(id+"F2.wireOp",EDGE,"E4.MirrorCS"),sQuery(id+"F2.wireOp",EDGE,"E5.MirrorCS")])]});
            var Q8;
            Q8=makeQuery(id+"F3.opExtrude","CAP_EDGE",EDGE,{"disambiguationData":[OSD([sQuery(id+"F2.wireOp",EDGE,"E4.MirrorCS")])],"isStart":false});
            var Q9;
            Q9=makeQuery(id+"F3.opExtrude","SWEPT_EDGE",EDGE,{"disambiguationData":[OSD([sQuery(id+"F0.wireOp",EDGE,"E0.bottom"),sQuery(id+"F2.wireOp",EDGE,"E4.MirrorCS"),sQuery(id+"F2.wireOp",EDGE,"E6.MirrorCS")])]});
            var Q10;
            Q10=makeQuery(id+"F5.opPattern","COPY",EDGE,{"derivedFrom":makeQuery(id+"F3.opExtrude","CAP_EDGE",EDGE,{"disambiguationData":[OSD([sQuery(id+"F2.wireOp",EDGE,"E1.right")])],"isStart":false}),"instanceName":"1"});
            var Q11;
            Q11=makeQuery(id+"F5.opPattern","COPY",EDGE,{"derivedFrom":makeQuery(id+"F3.opExtrude","CAP_EDGE",EDGE,{"disambiguationData":[OSD([sQuery(id+"F2.wireOp",EDGE,"E1.left")])],"isStart":false}),"instanceName":"1"});
            var Q12;
            Q12=makeQuery(id+"F5.opPattern","COPY",EDGE,{"derivedFrom":makeQuery(id+"F3.opExtrude","CAP_EDGE",EDGE,{"disambiguationData":[OSD([sQuery(id+"F2.wireOp",EDGE,"E1.top")])],"isStart":false}),"instanceName":"1"});
            var Q13;
            Q13=makeQuery(id+"F5.opPattern","COPY",EDGE,{"derivedFrom":makeQuery(id+"F3.opExtrude","SWEPT_EDGE",EDGE,{"disambiguationData":[OSD([sQuery(id+"F0.wireOp",EDGE,"E0.bottom"),sQuery(id+"F2.wireOp",EDGE,"E1.top"),sQuery(id+"F2.wireOp",EDGE,"E1.left")])]}),"instanceName":"1"});
            var Q14;
            Q14=makeQuery(id+"F5.opPattern","COPY",EDGE,{"derivedFrom":makeQuery(id+"F3.opExtrude","SWEPT_EDGE",EDGE,{"disambiguationData":[OSD([sQuery(id+"F0.wireOp",EDGE,"E0.bottom"),sQuery(id+"F2.wireOp",EDGE,"E1.top"),sQuery(id+"F2.wireOp",EDGE,"E1.right")])]}),"instanceName":"1"});
            var Q15;
            Q15=makeQuery(id+"F3.opExtrude","SWEPT_EDGE",EDGE,{"disambiguationData":[OSD([sQuery(id+"F0.wireOp",EDGE,"E0.bottom"),sQuery(id+"F2.wireOp",EDGE,"E1.top"),sQuery(id+"F2.wireOp",EDGE,"E1.left")])]});
            var Q16;
            Q16=makeQuery(id+"F3.opExtrude","CAP_EDGE",EDGE,{"disambiguationData":[OSD([sQuery(id+"F2.wireOp",EDGE,"E1.top")])],"isStart":false});
            var Q17;
            Q17=makeQuery(id+"F3.opExtrude","SWEPT_EDGE",EDGE,{"disambiguationData":[OSD([sQuery(id+"F0.wireOp",EDGE,"E0.bottom"),sQuery(id+"F2.wireOp",EDGE,"E1.top"),sQuery(id+"F2.wireOp",EDGE,"E1.right")])]});
            var Q18;
            Q18=makeQuery(id+"F3.opExtrude","CAP_EDGE",EDGE,{"disambiguationData":[OSD([sQuery(id+"F2.wireOp",EDGE,"E1.right")])],"isStart":false});
            var Q19;
            Q19=makeQuery(id+"F3.opExtrude","CAP_EDGE",EDGE,{"disambiguationData":[OSD([sQuery(id+"F2.wireOp",EDGE,"E1.left")])],"isStart":false});
            fillet(context, id + "F28", {"entities" : qUnion([Q0, Q1, Q2, Q3, Q4, Q5, Q6, Q7, Q8, Q9, Q10, Q11, Q12, Q13, Q14, Q15, Q16, Q17, Q18, Q19]), "radius" : 1.5 * mm, "tangentPropagation" : true, "allowEdgeOverflow" : false});
        }
        {
            var Q0;
            Q0=makeQuery(id+"F18.opExtrude","SWEPT_EDGE",EDGE,{"disambiguationData":[OSD([sQuery(id+"F0.wireOp",EDGE,"E0.top"),sQuery(id+"F17.wireOp",EDGE,"E53.MirrorCS"),sQuery(id+"F17.wireOp",EDGE,"E55.MirrorCS")])]});
            var Q1;
            Q1=makeQuery(id+"F18.opExtrude","SWEPT_EDGE",EDGE,{"disambiguationData":[OSD([sQuery(id+"F0.wireOp",EDGE,"E0.top"),sQuery(id+"F17.wireOp",EDGE,"E52.MirrorCS"),sQuery(id+"F17.wireOp",EDGE,"E55.MirrorCS")])]});
            var Q2;
            Q2=makeQuery(id+"F18.opExtrude","SWEPT_EDGE",EDGE,{"disambiguationData":[OSD([sQuery(id+"F0.wireOp",EDGE,"E0.top"),sQuery(id+"F17.wireOp",EDGE,"E53.MirrorCS"),sQuery(id+"F17.wireOp",EDGE,"E54.MirrorCS")])]});
            var Q3;
            Q3=makeQuery(id+"F18.opExtrude","SWEPT_EDGE",EDGE,{"disambiguationData":[OSD([sQuery(id+"F0.wireOp",EDGE,"E0.top"),sQuery(id+"F17.wireOp",EDGE,"E52.MirrorCS"),sQuery(id+"F17.wireOp",EDGE,"E54.MirrorCS")])]});
            var Q4;
            Q4=makeQuery(id+"F18.opExtrude","SWEPT_EDGE",EDGE,{"disambiguationData":[OSD([sQuery(id+"F0.wireOp",EDGE,"E0.top"),sQuery(id+"F17.wireOp",EDGE,"E51.top"),sQuery(id+"F17.wireOp",EDGE,"E51.left")])]});
            var Q5;
            Q5=makeQuery(id+"F18.opExtrude","SWEPT_EDGE",EDGE,{"disambiguationData":[OSD([sQuery(id+"F0.wireOp",EDGE,"E0.top"),sQuery(id+"F17.wireOp",EDGE,"E51.top"),sQuery(id+"F17.wireOp",EDGE,"E51.right")])]});
            var Q6;
            Q6=makeQuery(id+"F18.opExtrude","SWEPT_EDGE",EDGE,{"disambiguationData":[OSD([sQuery(id+"F0.wireOp",EDGE,"E0.top"),sQuery(id+"F17.wireOp",EDGE,"E51.bottom"),sQuery(id+"F17.wireOp",EDGE,"E51.left")])]});
            var Q7;
            Q7=makeQuery(id+"F18.opExtrude","SWEPT_EDGE",EDGE,{"disambiguationData":[OSD([sQuery(id+"F0.wireOp",EDGE,"E0.top"),sQuery(id+"F17.wireOp",EDGE,"E51.bottom"),sQuery(id+"F17.wireOp",EDGE,"E51.right")])]});
            var Q8;
            Q8=makeQuery(id+"F9.opExtrude","SWEPT_EDGE",EDGE,{"disambiguationData":[OSD([sQuery(id+"F8.wireOp",EDGE,"E42.bottom"),sQuery(id+"F8.wireOp",EDGE,"E45.0")])]});
            var Q9;
            Q9=makeQuery(id+"F9.opExtrude","SWEPT_EDGE",EDGE,{"disambiguationData":[OSD([sQuery(id+"F0.wireOp",EDGE,"E0.bottom"),sQuery(id+"F8.wireOp",EDGE,"E42.bottom"),sQuery(id+"F8.wireOp",EDGE,"E42.left")])]});
            var Q10;
            Q10=makeQuery(id+"F9.opExtrude","SWEPT_EDGE",EDGE,{"disambiguationData":[OSD([sQuery(id+"F0.wireOp",EDGE,"E0.bottom"),sQuery(id+"F8.wireOp",EDGE,"E42.top"),sQuery(id+"F8.wireOp",EDGE,"E42.left")])]});
            var Q11;
            Q11=makeQuery(id+"F9.opExtrude","SWEPT_EDGE",EDGE,{"disambiguationData":[OSD([sQuery(id+"F8.wireOp",EDGE,"E42.top"),sQuery(id+"F8.wireOp",EDGE,"E45.0")])]});
            var Q12;
            Q12=makeQuery(id+"F9.opExtrude","SWEPT_EDGE",EDGE,{"disambiguationData":[OSD([sQuery(id+"F8.wireOp",EDGE,"E42.bottom"),sQuery(id+"F8.wireOp",EDGE,"E43.0")])]});
            var Q13;
            Q13=makeQuery(id+"F9.opExtrude","SWEPT_EDGE",EDGE,{"disambiguationData":[OSD([sQuery(id+"F0.wireOp",EDGE,"E0.bottom"),sQuery(id+"F8.wireOp",EDGE,"E42.bottom"),sQuery(id+"F8.wireOp",EDGE,"E42.right")])]});
            var Q14;
            Q14=makeQuery(id+"F9.opExtrude","SWEPT_EDGE",EDGE,{"disambiguationData":[OSD([sQuery(id+"F8.wireOp",EDGE,"E42.top"),sQuery(id+"F8.wireOp",EDGE,"E43.0")])]});
            var Q15;
            Q15=makeQuery(id+"F9.opExtrude","SWEPT_EDGE",EDGE,{"disambiguationData":[OSD([sQuery(id+"F0.wireOp",EDGE,"E0.bottom"),sQuery(id+"F8.wireOp",EDGE,"E42.top"),sQuery(id+"F8.wireOp",EDGE,"E42.right")])]});
            fillet(context, id + "F29", {"entities" : qUnion([Q0, Q1, Q2, Q3, Q4, Q5, Q6, Q7, Q8, Q9, Q10, Q11, Q12, Q13, Q14, Q15]), "radius" : 2 * mm, "tangentPropagation" : true, "allowEdgeOverflow" : false});
        }
        {
            var Q0;
            Q0=makeQuery(id+"F1.opExtrude","SWEPT_FACE",FACE,{"disambiguationData":[OSD([sQuery(id+"F0.wireOp",EDGE,"E0.left")])]});
            var sketch = newSketch(context, id + "F30", { "sketchPlane" : qUnion([Q0])});
            skLineSegment(sketch, "E59.bottom", {"start": v(0, 50) * mm, "end": v(-1160, 50) * mm});
            skLineSegment(sketch, "E59.top", {"start": v(0, 230) * mm, "end": v(-1160, 230) * mm});
            skLineSegment(sketch, "E59.left", {"start": v(0, 50) * mm, "end": v(0, 230) * mm});
            skLineSegment(sketch, "E59.right", {"start": v(-1160, 50) * mm, "end": v(-1160, 230) * mm});
            skSolve(sketch);
        }
        {
            var Q0;
            Q0 = qSketchRegion(id + "F30", true);
            extrude(context, id + "F31", {"entities" : qUnion([Q0]), "depth" : 65 * mm, "offsetDistance" : 25 * mm});
        }
        {
            var Q0;
            Q0=makeQuery(id+"F31.opExtrude","SWEPT_EDGE",EDGE,{"disambiguationData":[OSD([sQuery(id+"F0.wireOp",EDGE,"E0.top"),sQuery(id+"F0.wireOp",EDGE,"E0.left"),sQuery(id+"F30.wireOp",EDGE,"E59.top"),sQuery(id+"F30.wireOp",EDGE,"E59.right")])]});
            var Q1;
            Q1=makeQuery(id+"F31.opExtrude","SWEPT_EDGE",EDGE,{"disambiguationData":[OSD([sQuery(id+"F0.wireOp",EDGE,"E0.top"),sQuery(id+"F0.wireOp",EDGE,"E0.left"),sQuery(id+"F30.wireOp",EDGE,"E59.bottom"),sQuery(id+"F30.wireOp",EDGE,"E59.right")])]});
            var Q2;
            Q2=makeQuery(id+"F31.opExtrude","CAP_EDGE",EDGE,{"disambiguationData":[OSD([sQuery(id+"F30.wireOp",EDGE,"E59.right")])],"isStart":false});
            var Q3;
            Q3=makeQuery(id+"F31.opExtrude","CAP_EDGE",EDGE,{"disambiguationData":[OSD([sQuery(id+"F30.wireOp",EDGE,"E59.top")])],"isStart":false});
            var Q4;
            Q4=makeQuery(id+"F31.opExtrude","CAP_EDGE",EDGE,{"disambiguationData":[OSD([sQuery(id+"F30.wireOp",EDGE,"E59.bottom")])],"isStart":false});
            var Q5;
            Q5=makeQuery(id+"F31.opExtrude","SWEPT_EDGE",EDGE,{"disambiguationData":[OSD([sQuery(id+"F0.wireOp",EDGE,"E0.bottom"),sQuery(id+"F0.wireOp",EDGE,"E0.left"),sQuery(id+"F30.wireOp",EDGE,"E59.top"),sQuery(id+"F30.wireOp",EDGE,"E59.left")])]});
            var Q6;
            Q6=makeQuery(id+"F31.opExtrude","SWEPT_EDGE",EDGE,{"disambiguationData":[OSD([sQuery(id+"F0.wireOp",EDGE,"E0.bottom"),sQuery(id+"F0.wireOp",EDGE,"E0.left"),sQuery(id+"F30.wireOp",EDGE,"E59.bottom"),sQuery(id+"F30.wireOp",EDGE,"E59.left")])]});
            var Q7;
            Q7=makeQuery(id+"F31.opExtrude","CAP_EDGE",EDGE,{"disambiguationData":[OSD([sQuery(id+"F30.wireOp",EDGE,"E59.left")])],"isStart":false});
            fillet(context, id + "F32", {"entities" : qUnion([Q0, Q1, Q2, Q3, Q4, Q5, Q6, Q7]), "radius" : 2 * mm, "tangentPropagation" : true, "allowEdgeOverflow" : false});
        }
        {
            var Q0;
            Q0=makeQuery(id+"F1.opExtrude","CAP_EDGE",EDGE,{"disambiguationData":[OSD([sQuery(id+"F0.wireOp",EDGE,"E0.left")])],"isStart":false});
            var Q1;
            Q1=makeQuery(id+"F1.opExtrude","CAP_EDGE",EDGE,{"disambiguationData":[OSD([sQuery(id+"F0.wireOp",EDGE,"E0.right")])],"isStart":false});
            var Q2;
            Q2=makeQuery(id+"F1.opExtrude","CAP_EDGE",EDGE,{"disambiguationData":[OSD([sQuery(id+"F0.wireOp",EDGE,"E0.top")])],"isStart":false});
            var Q3;
            Q3=makeQuery(id+"F1.opExtrude","CAP_EDGE",EDGE,{"disambiguationData":[OSD([sQuery(id+"F0.wireOp",EDGE,"E0.left")])],"isStart":true});
            var Q4;
            Q4=makeQuery(id+"F1.opExtrude","CAP_EDGE",EDGE,{"disambiguationData":[OSD([sQuery(id+"F0.wireOp",EDGE,"E0.right")])],"isStart":true});
            var Q5;
            Q5=makeQuery(id+"F1.opExtrude","CAP_EDGE",EDGE,{"disambiguationData":[OSD([sQuery(id+"F0.wireOp",EDGE,"E0.bottom")])],"isStart":true});
            var Q6;
            Q6=makeQuery(id+"F1.opExtrude","CAP_EDGE",EDGE,{"disambiguationData":[OSD([sQuery(id+"F0.wireOp",EDGE,"E0.top")])],"isStart":true});
            var Q7;
            Q7=makeQuery(id+"F1.opExtrude","CAP_EDGE",EDGE,{"disambiguationData":[OSD([sQuery(id+"F0.wireOp",EDGE,"E0.bottom")])],"isStart":false});
            fillet(context, id + "F33", {"entities" : qUnion([Q0, Q1, Q2, Q3, Q4, Q5, Q6, Q7]), "radius" : 5 * mm, "tangentPropagation" : true, "allowEdgeOverflow" : false});
        }
        {
            var Q0;
            Q0=makeQuery(id+"F1.opExtrude","SWEPT_FACE",FACE,{"disambiguationData":[OSD([sQuery(id+"F0.wireOp",EDGE,"E0.right")])]});
            var sketch = newSketch(context, id + "F34", { "sketchPlane" : qUnion([Q0])});
            skLineSegment(sketch, "E60.bottom", {"start": v(0, 15) * mm, "end": v(1160, 15) * mm});
            skLineSegment(sketch, "E60.top", {"start": v(0, 271) * mm, "end": v(1160, 271) * mm});
            skLineSegment(sketch, "E60.left", {"start": v(0, 15) * mm, "end": v(0, 271) * mm});
            skLineSegment(sketch, "E60.right", {"start": v(1160, 15) * mm, "end": v(1160, 271) * mm});
            skSolve(sketch);
        }
        {
            var Q0;
            Q0 = qSketchRegion(id + "F34", true);
            extrude(context, id + "F35", {"entities" : qUnion([Q0]), "depth" : 185 * mm, "offsetDistance" : 25 * mm});
        }
        {
            var Q0;
            Q0=makeQuery(id+"F35.opExtrude","CAP_EDGE",EDGE,{"disambiguationData":[OSD([sQuery(id+"F34.wireOp",EDGE,"E60.top")])],"isStart":false});
            var Q1;
            Q1=makeQuery(id+"F35.opExtrude","CAP_EDGE",EDGE,{"disambiguationData":[OSD([sQuery(id+"F34.wireOp",EDGE,"E60.bottom")])],"isStart":false});
            var Q2;
            Q2=makeQuery(id+"F35.opExtrude","CAP_EDGE",EDGE,{"disambiguationData":[OSD([sQuery(id+"F34.wireOp",EDGE,"E60.right")])],"isStart":false});
            var Q3;
            Q3=makeQuery(id+"F35.opExtrude","SWEPT_EDGE",EDGE,{"disambiguationData":[OSD([sQuery(id+"F0.wireOp",EDGE,"E0.top"),sQuery(id+"F0.wireOp",EDGE,"E0.right"),sQuery(id+"F34.wireOp",EDGE,"E60.top"),sQuery(id+"F34.wireOp",EDGE,"E60.right")])]});
            var Q4;
            Q4=makeQuery(id+"F35.opExtrude","SWEPT_EDGE",EDGE,{"disambiguationData":[OSD([sQuery(id+"F0.wireOp",EDGE,"E0.top"),sQuery(id+"F0.wireOp",EDGE,"E0.right"),sQuery(id+"F34.wireOp",EDGE,"E60.bottom"),sQuery(id+"F34.wireOp",EDGE,"E60.right")])]});
            var Q5;
            Q5=makeQuery(id+"F35.opExtrude","SWEPT_EDGE",EDGE,{"disambiguationData":[OSD([sQuery(id+"F0.wireOp",EDGE,"E0.bottom"),sQuery(id+"F0.wireOp",EDGE,"E0.right"),sQuery(id+"F34.wireOp",EDGE,"E60.top"),sQuery(id+"F34.wireOp",EDGE,"E60.left")])]});
            var Q6;
            Q6=makeQuery(id+"F35.opExtrude","SWEPT_EDGE",EDGE,{"disambiguationData":[OSD([sQuery(id+"F0.wireOp",EDGE,"E0.bottom"),sQuery(id+"F0.wireOp",EDGE,"E0.right"),sQuery(id+"F34.wireOp",EDGE,"E60.bottom"),sQuery(id+"F34.wireOp",EDGE,"E60.left")])]});
            var Q7;
            Q7=makeQuery(id+"F35.opExtrude","CAP_EDGE",EDGE,{"disambiguationData":[OSD([sQuery(id+"F34.wireOp",EDGE,"E60.left")])],"isStart":false});
            fillet(context, id + "F36", {"entities" : qUnion([Q0, Q1, Q2, Q3, Q4, Q5, Q6, Q7]), "radius" : 2 * mm, "tangentPropagation" : true, "allowEdgeOverflow" : false});
        }
        {
            var Q0;
            Q0=makeQuery(id+"F35.opExtrude","CAP_FACE",FACE,{"disambiguationData":[OSD([sQuery(id+"F34.wireOp",EDGE,"E60.bottom"),sQuery(id+"F34.wireOp",EDGE,"E60.top"),sQuery(id+"F34.wireOp",EDGE,"E60.left"),sQuery(id+"F34.wireOp",EDGE,"E60.right")])],"isStart":false});
            var sketch = newSketch(context, id + "F37", { "sketchPlane" : qUnion([Q0])});
            skCircle(sketch, "E61", {"center": v(182, 85) * mm, "radius": 57.15 * mm});
            skCircle(sketch, "E62", {"center": v(978, 201) * mm, "radius": 57.15 * mm});
            skSolve(sketch);
        }
        {
            var Q0;
            Q0 = qSketchRegion(id + "F37", true);
            extrude(context, id + "F38", {"entities" : qUnion([Q0]), "depth" : 128 * mm, "offsetDistance" : 25 * mm});
        }
        {
            var Q0;
            Q0=makeQuery(id+"F38.opExtrude","CAP_FACE",FACE,{"disambiguationData":[OSD([sQuery(id+"F37.wireOp",EDGE,"E61")])],"isStart":false});
            var sketch = newSketch(context, id + "F39", { "sketchPlane" : qUnion([Q0])});
            skCircle(sketch, "E63", {"center": v(182, 85) * mm, "radius": 110 * mm});
            skCircle(sketch, "E64", {"center": v(978, 201) * mm, "radius": 110 * mm});
            skSolve(sketch);
        }
        {
            var Q0;
            Q0 = qSketchRegion(id + "F39", true);
            extrude(context, id + "F40", {"entities" : qUnion([Q0]), "depth" : 22 * mm, "offsetDistance" : 25 * mm});
        }
        {
            var Q0;
            Q0=makeQuery(id+"F40.opExtrude","CAP_EDGE",EDGE,{"disambiguationData":[OSD([sQuery(id+"F39.wireOp",EDGE,"E63")])],"isStart":true});
            var Q1;
            Q1=makeQuery(id+"F40.opExtrude","CAP_EDGE",EDGE,{"disambiguationData":[OSD([sQuery(id+"F39.wireOp",EDGE,"E63")])],"isStart":false});
            var Q2;
            Q2=makeQuery(id+"F40.opExtrude","CAP_EDGE",EDGE,{"disambiguationData":[OSD([sQuery(id+"F39.wireOp",EDGE,"E64")])],"isStart":true});
            var Q3;
            Q3=makeQuery(id+"F40.opExtrude","CAP_EDGE",EDGE,{"disambiguationData":[OSD([sQuery(id+"F39.wireOp",EDGE,"E64")])],"isStart":false});
            fillet(context, id + "F41", {"entities" : qUnion([Q0, Q1, Q2, Q3]), "radius" : 1 * mm, "tangentPropagation" : true, "allowEdgeOverflow" : false});
        }
        {
            var Q0;
            Q0=makeQuery(id+"F40.opExtrude","CAP_FACE",FACE,{"disambiguationData":[OSD([sQuery(id+"F39.wireOp",EDGE,"E63")])],"isStart":false});
            var sketch = newSketch(context, id + "F42", { "sketchPlane" : qUnion([Q0])});
            skCircle(sketch, "E65", {"center": v(182, 85) * mm, "radius": 56.2 * mm});
            skCircle(sketch, "E66", {"center": v(978, 201) * mm, "radius": 56.2 * mm});
            skSolve(sketch);
        }
        {
            var Q0;
            Q0 = qSketchRegion(id + "F42", true);
            var Q1;
            Q1=makeQuery(id+"F35.opExtrude","CAP_FACE",FACE,{"disambiguationData":[OSD([sQuery(id+"F34.wireOp",EDGE,"E60.bottom"),sQuery(id+"F34.wireOp",EDGE,"E60.top"),sQuery(id+"F34.wireOp",EDGE,"E60.left"),sQuery(id+"F34.wireOp",EDGE,"E60.right")])],"isStart":false});
            extrude(context, id + "F43", {"entities" : qUnion([Q0]), "operationType" : NewBodyOperationType.REMOVE, "endBound" : BoundingType.UP_TO_SURFACE, "oppositeDirection" : true, "depth" : 25 * mm, "endBoundEntityFace" : qUnion([Q1]), "offsetDistance" : 25 * mm});
        }
        {
            var Q0;
            Q0=makeQuery(id+"F40.opExtrude","CAP_FACE",FACE,{"disambiguationData":[OSD([sQuery(id+"F39.wireOp",EDGE,"E63")])],"isStart":false});
            var sketch = newSketch(context, id + "F44", { "sketchPlane" : qUnion([Q0])});
            skCircle(sketch, "E67", {"center": v(216.44, 168.15) * mm, "radius": 9 * mm});
            skCircle(sketch, "E68.1.0", {"center": v(147.56, 168.15) * mm, "radius": 9 * mm});
            skCircle(sketch, "E68.2.0", {"center": v(98.85, 119.44) * mm, "radius": 9 * mm});
            skCircle(sketch, "E68.3.0", {"center": v(98.85, 50.56) * mm, "radius": 9 * mm});
            skCircle(sketch, "E68.4.0", {"center": v(147.56, 1.85) * mm, "radius": 9 * mm});
            skCircle(sketch, "E68.5.0", {"center": v(216.44, 1.85) * mm, "radius": 9 * mm});
            skCircle(sketch, "E68.6.0", {"center": v(265.15, 50.56) * mm, "radius": 9 * mm});
            skCircle(sketch, "E68.7.0", {"center": v(265.15, 119.44) * mm, "radius": 9 * mm});
            skPoint(sketch, "E68.center", {"position": v(182, 85) * mm});
            skCircle(sketch, "E69", {"center": v(1012.44, 284.15) * mm, "radius": 9 * mm});
            skCircle(sketch, "E70.1.0", {"center": v(943.56, 284.15) * mm, "radius": 9 * mm});
            skCircle(sketch, "E70.2.0", {"center": v(894.85, 235.44) * mm, "radius": 9 * mm});
            skCircle(sketch, "E70.3.0", {"center": v(894.85, 166.56) * mm, "radius": 9 * mm});
            skCircle(sketch, "E70.4.0", {"center": v(943.56, 117.85) * mm, "radius": 9 * mm});
            skCircle(sketch, "E70.5.0", {"center": v(1012.44, 117.85) * mm, "radius": 9 * mm});
            skCircle(sketch, "E70.6.0", {"center": v(1061.15, 166.56) * mm, "radius": 9 * mm});
            skCircle(sketch, "E70.7.0", {"center": v(1061.15, 235.44) * mm, "radius": 9 * mm});
            skPoint(sketch, "E70.center", {"position": v(978, 201) * mm});
            skSolve(sketch);
        }
        {
            var Q0;
            Q0 = qSketchRegion(id + "F44", true);
            extrude(context, id + "F45", {"entities" : qUnion([Q0]), "operationType" : NewBodyOperationType.REMOVE, "endBound" : BoundingType.UP_TO_NEXT, "oppositeDirection" : true, "depth" : 25 * mm, "offsetDistance" : 25 * mm});
        }
        {
            var Q0;
            Q0=makeQuery(id+"F40.opExtrude","CAP_FACE",FACE,{"disambiguationData":[OSD([sQuery(id+"F39.wireOp",EDGE,"E63")])],"isStart":false});
            var Q1;
            Q1=makeQuery(id+"F40.opExtrude","CAP_FACE",FACE,{"disambiguationData":[OSD([sQuery(id+"F39.wireOp",EDGE,"E63")])],"isStart":true});
            var Q2;
            Q2=makeQuery(id+"F40.opExtrude","CAP_FACE",FACE,{"disambiguationData":[OSD([sQuery(id+"F39.wireOp",EDGE,"E64")])],"isStart":true});
            var Q3;
            Q3=makeQuery(id+"F40.opExtrude","CAP_FACE",FACE,{"disambiguationData":[OSD([sQuery(id+"F39.wireOp",EDGE,"E64")])],"isStart":false});
            fillet(context, id + "F46", {"entities" : qUnion([Q0, Q1, Q2, Q3]), "radius" : 1 * mm, "tangentPropagation" : true, "allowEdgeOverflow" : false});
        }
    });
